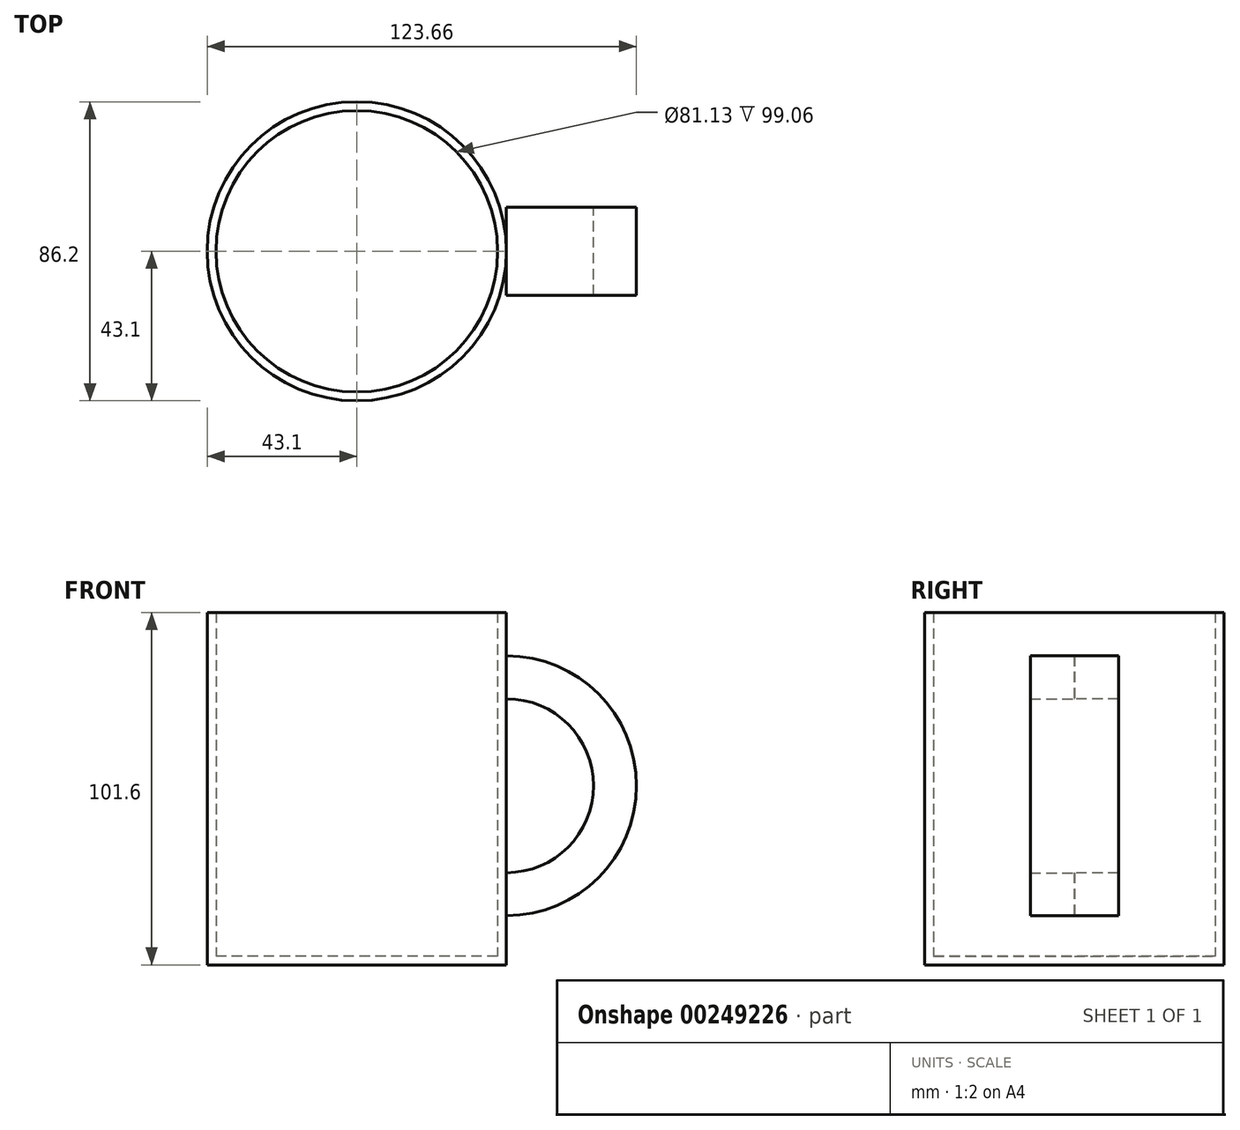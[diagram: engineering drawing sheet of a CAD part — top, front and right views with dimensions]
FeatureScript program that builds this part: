
annotation { "Feature Type Name" : "Feature", "Feature Type Description" : "" }
export const myFeature = defineFeature(function(context is Context, id is Id, definition is map)
    precondition{}
    {
        {
            var Q0;
            Q0=qCreatedBy(makeId("Top.planeOp"),FACE);
            var sketch = newSketch(context, id + "F0", { "sketchPlane" : qUnion([Q0])});
            skCircle(sketch, "E0", {"center": v(0, 0) * mm, "radius": 43.1 * mm});
            skSolve(sketch);
        }
        {
            var Q0;
            Q0 = qSketchRegion(id + "F0", true);
            extrude(context, id + "F1", {"entities" : qUnion([Q0]), "depth" : 101.6 * mm});
        }
        {
            var Q0;
            Q0=qCreatedBy(makeId("Front.planeOp"),FACE);
            var sketch = newSketch(context, id + "F2", { "sketchPlane" : qUnion([Q0])});
            skArc(sketch, "E1", {"start": v(43.1, 14.17) * mm, "mid": v(80.56, 51.63) * mm, "end": v(43.1, 89.1) * mm});
            skArc(sketch, "E2", {"start": v(43.1, 26.56) * mm, "mid": v(68.18, 51.63) * mm, "end": v(43.1, 76.7) * mm});
            skLineSegment(sketch, "E3", {"start": v(43.1, 89.1) * mm, "end": v(43.1, 14.17) * mm});
            skSolve(sketch);
        }
        {
            var Q0;
            Q0=makeQuery(id+"F1.opExtrude","CAP_FACE",FACE,{"disambiguationData":[OSD([sQuery(id+"F0.wireOp",EDGE,"E0")])],"isStart":false});
            shell(context, id + "F3", {"entities" : qUnion([Q0]), "thickness" : 2.54 * mm});
        }
        {
            var Q0;
            {var subQ0=sQuery(id+"F2.wireOp",EDGE,"E1");Q0=makeQuery(id+"F2.imprint","IMPRINT",FACE,{"disambiguationData":[TD([[makeQuery(id+"F2.imprint","IMPRINT",EDGE,{"derivedFrom":subQ0}),1.0]])]});}
            extrude(context, id + "F4", {"entities" : qUnion([Q0]), "operationType" : NewBodyOperationType.ADD, "depth" : 12.7 * mm});
        }
        {
            var Q0;
            Q0=makeQuery(id+"F4.opExtrude","CAP_FACE",FACE,{"disambiguationData":[OSD([sQuery(id+"F2.wireOp",EDGE,"E1"),sQuery(id+"F2.wireOp",EDGE,"E2"),sQuery(id+"F2.wireOp",EDGE,"E3")])],"isStart":true});
            extrude(context, id + "F5", {"entities" : qUnion([Q0]), "operationType" : NewBodyOperationType.ADD, "depth" : 12.7 * mm});
        }
    });
